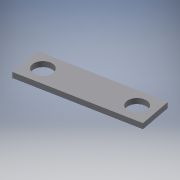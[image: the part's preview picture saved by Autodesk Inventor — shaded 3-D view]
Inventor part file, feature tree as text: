
AUTODESK INVENTOR PART (.ipt)
format: ipt  version: 2018 (Build 220112000, 112)  size: 136,704 bytes
history: native  units: mm
features: other x3, extrude x2, sketch x2, fillet x1, reference x1
ambient origin geometry x8: Origin, YZ Plane, XZ Plane, XY Plane, X Axis, Y Axis, Z Axis, Center Point
bodies: Solid1 (feature_tree)
feature tree (9):
  extrude  "Extrusion1"  Depth=3.5mm
  extrude  "Extrusion2"  Depth=1.0mm
  fillet  "Fillet1"  Radius=3.0mm
  sketch  "Sketch1"  dims[d0=3.5mm d1=3.5mm]
  sketch  "Sketch2"  dims[d2=90.0deg d3=3.0mm d4=3.0mm d5=180.0deg d6=3.0mm d7=1.0mm d8=0.0mm d9=1.0mm d10=0.0mm d11=1.0mm]
  reference  "Reference3"
  other  "<userpath>\OneDrive\Documents\Inventor\TSA\2018\Animatronics\Tortoise\Turtle3.iam"
  other  "Turtle3.iam"
  other  "HeadBottom:1"
